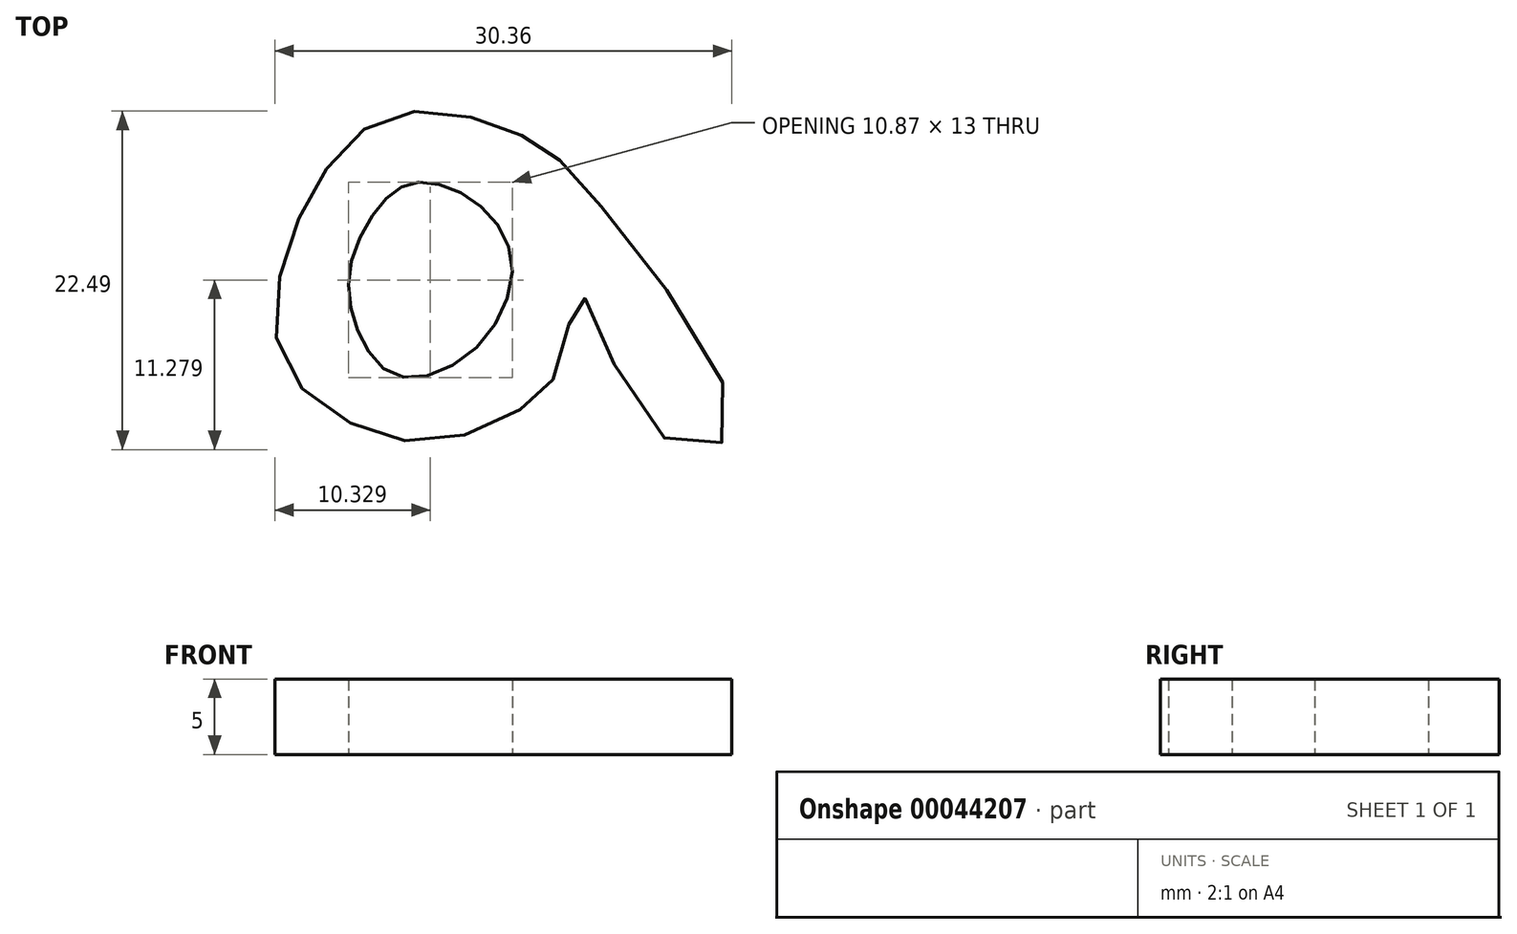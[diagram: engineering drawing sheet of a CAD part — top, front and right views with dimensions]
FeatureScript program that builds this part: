
annotation { "Feature Type Name" : "Feature", "Feature Type Description" : "" }
export const myFeature = defineFeature(function(context is Context, id is Id, definition is map)
    precondition{}
    {
        {
            var Q0;
            Q0=qCreatedBy(makeId("Top.planeOp"),FACE);
            var sketch = newSketch(context, id + "F0", { "sketchPlane" : qUnion([Q0])});
            skFitSpline(sketch, "E0", {"points": [v(-33.35, 34.83) * mm, v(-37.38, 38.86) * mm, v(-41.95, 40.74) * mm, v(-47.6, 40.74) * mm, v(-51.64, 37.25) * mm, v(-54.33, 31.6) * mm, v(-54.6, 24.88) * mm, v(-50.3, 20.57) * mm, v(-44.38, 19.23) * mm, v(-38.19, 21.65) * mm, v(-36.04, 24.6) * mm, v(-34.7, 28.91) * mm, v(-29.58, 19.77) * mm, v(-24.74, 20.04) * mm, v(-33.35, 34.83) * mm]});
            skFitSpline(sketch, "E1", {"points": [v(-45.45, 36.44) * mm, v(-41.69, 35.1) * mm, v(-39.27, 31.06) * mm, v(-41.69, 25.41) * mm, v(-46.8, 23.53) * mm, v(-49.49, 26.5) * mm, v(-50.02, 30.8) * mm, v(-47.87, 35.1) * mm, v(-45.45, 36.44) * mm]});
            skSolve(sketch);
        }
        {
            var Q0;
            Q0=makeQuery(id+"F0.imprint","IMPRINT",FACE,{"disambiguationData":[TD([[makeQuery(id+"F0.imprint","IMPRINT",EDGE,{"derivedFrom":sQuery(id+"F0.wireOp",EDGE,"E0")}),1.0]])]});
            extrude(context, id + "F1", {"entities" : qUnion([Q0]), "depth" : 5 * mm});
        }
    });
